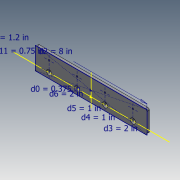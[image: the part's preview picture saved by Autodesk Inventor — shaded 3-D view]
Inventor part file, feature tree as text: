
AUTODESK INVENTOR PART (.ipt)
format: ipt  version: 2018.3 (Build 223284000, 284)  size: 125,440 bytes
history: native  units: in
note: dims shown in document units (in); Inventor stores cm internally (conversion verified against a paired STEP export)
features: hole x2, sketch x1, extrude x1, fillet x1
ambient origin geometry x8: Origin, YZ Plane, XZ Plane, XY Plane, X Axis, Y Axis, Z Axis, Center Point
bodies: Solid1 (feature_tree)
feature tree (5):
  sketch  "Sketch1"  dims[d0=0.375in d1=1.2in d2=8.0in d3=2.0in d4=1.0in d5=1.0in d6=2.0in d7=0.177in d8=0.0in d9=0.7874in d11=0.75in d12=0.3937in d14=1.0in d16=0.177in d17=0.75in d18=0.37in d19=0.25in d20=90.0deg d21=1.0in d22=0.8108in d23=0.123in d24=0.75in d25=0.37in d26=0.25in d27=90.0deg d28=1.0in d29=0.8108in d30=0.125in]
  extrude  "Extrusion1"  Depth=0.125in
  hole  "Hole1"  [1 undecoded]
  hole  "Hole2"  [1 undecoded]
  fillet  "Fillet1"  Radius=1.0in
note: 2 required parameter values undecoded (feature->parameter linkage not recoverable at this tier; creation-order binding heuristic only, values carry confidence <= 0.55)
